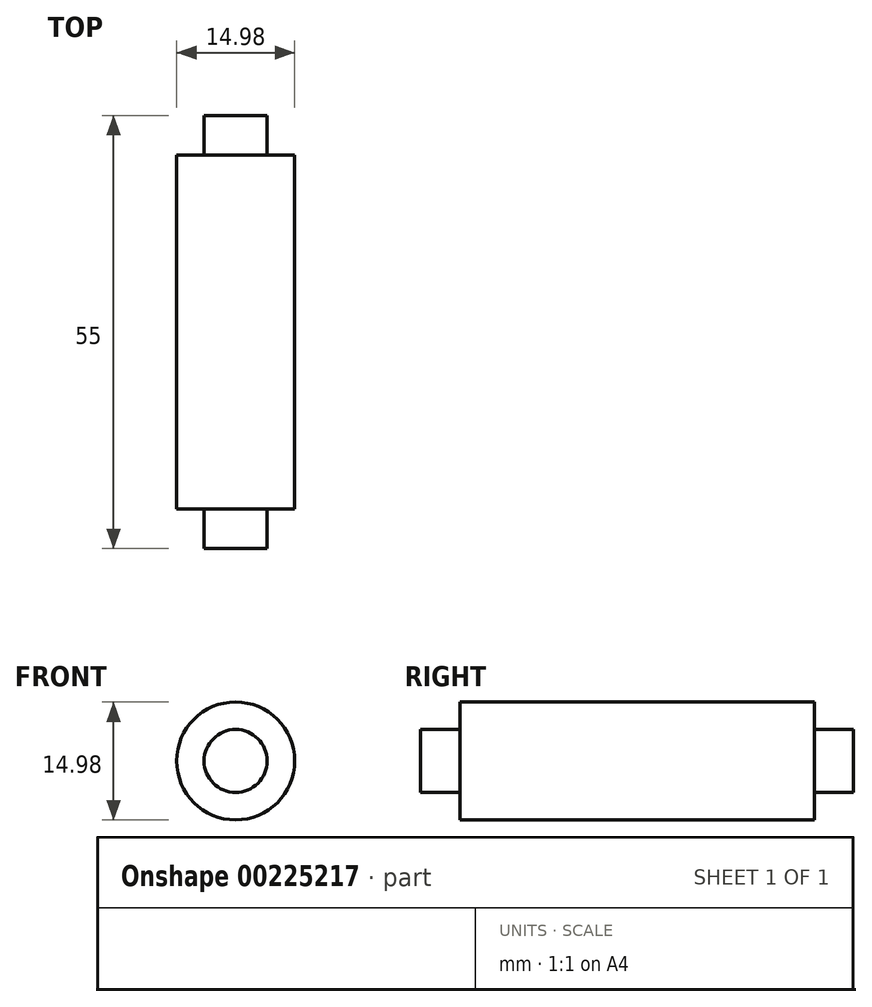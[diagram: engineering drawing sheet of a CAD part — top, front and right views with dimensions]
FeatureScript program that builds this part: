
annotation { "Feature Type Name" : "Feature", "Feature Type Description" : "" }
export const myFeature = defineFeature(function(context is Context, id is Id, definition is map)
    precondition{}
    {
        {
            var Q0;
            Q0=qCreatedBy(makeId("Front.planeOp"),FACE);
            var sketch = newSketch(context, id + "F0", { "sketchPlane" : qUnion([Q0])});
            skCircle(sketch, "E0", {"center": v(0, 0) * mm, "radius": 7.5 * mm});
            skSolve(sketch);
        }
        {
            var Q0;
            Q0=makeQuery(id+"F0.imprint","IMPRINT",FACE,{"disambiguationData":[TD([[makeQuery(id+"F0.imprint","IMPRINT",EDGE,{"derivedFrom":sQuery(id+"F0.wireOp",EDGE,"E0")}),1.0]])]});
            extrude(context, id + "F1", {"entities" : qUnion([Q0]), "endBound" : BoundingType.SYMMETRIC, "depth" : 45 * mm});
        }
        {
            var Q0;
            Q0=qCreatedBy(makeId("Front.planeOp"),FACE);
            var sketch = newSketch(context, id + "F2", { "sketchPlane" : qUnion([Q0])});
            skCircle(sketch, "E1", {"center": v(0, 0) * mm, "radius": 4 * mm});
            skSolve(sketch);
        }
        {
            var Q0;
            Q0=makeQuery(id+"F2.imprint","IMPRINT",FACE,{"disambiguationData":[TD([[makeQuery(id+"F2.imprint","IMPRINT",EDGE,{"derivedFrom":sQuery(id+"F2.wireOp",EDGE,"E1")}),1.0]])]});
            extrude(context, id + "F3", {"entities" : qUnion([Q0]), "operationType" : NewBodyOperationType.ADD, "endBound" : BoundingType.SYMMETRIC, "depth" : 55 * mm});
        }
    });
